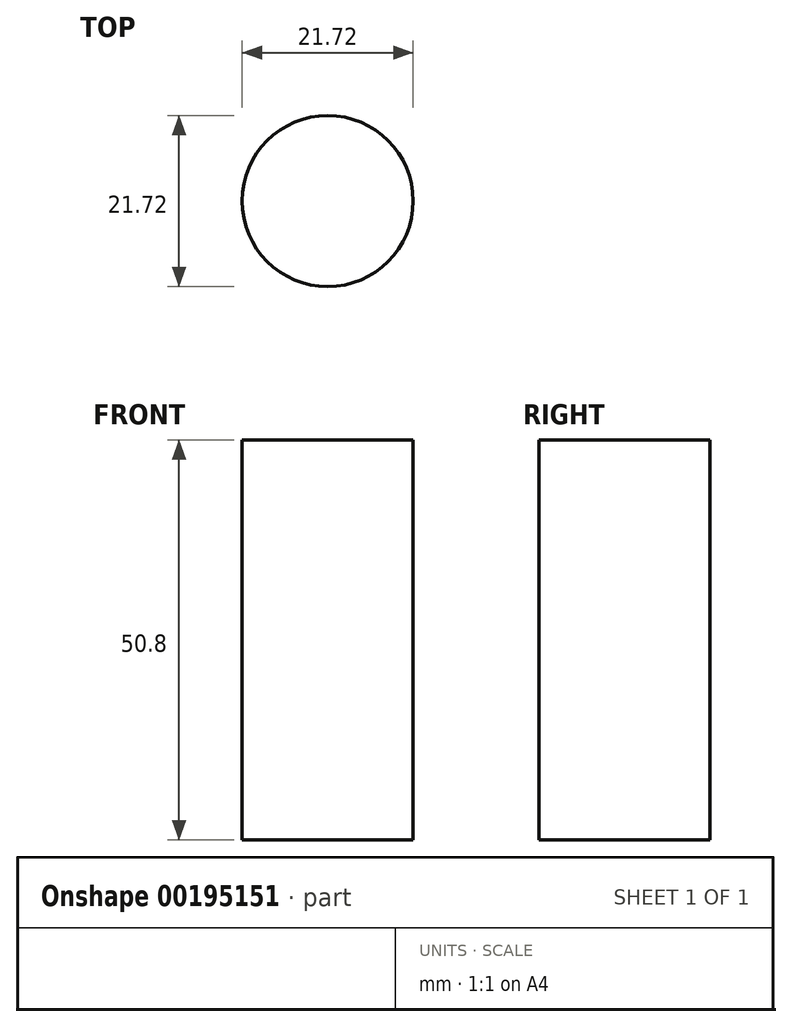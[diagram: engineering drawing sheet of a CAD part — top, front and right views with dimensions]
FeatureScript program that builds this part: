
annotation { "Feature Type Name" : "Feature", "Feature Type Description" : "" }
export const myFeature = defineFeature(function(context is Context, id is Id, definition is map)
    precondition{}
    {
        {
            var Q0;
            Q0=qCreatedBy(makeId("Top.planeOp"),FACE);
            var sketch = newSketch(context, id + "F0", { "sketchPlane" : qUnion([Q0])});
            skCircle(sketch, "E0", {"center": v(0, 0) * mm, "radius": 10.86 * mm});
            skSolve(sketch);
        }
        {
            var Q0;
            Q0=makeQuery(id+"F0.imprint","IMPRINT",FACE,{"disambiguationData":[TD([[makeQuery(id+"F0.imprint","IMPRINT",EDGE,{"derivedFrom":sQuery(id+"F0.wireOp",EDGE,"E0")}),1.0]])]});
            extrude(context, id + "F1", {"entities" : qUnion([Q0]), "depth" : 50.8 * mm});
        }
    });
